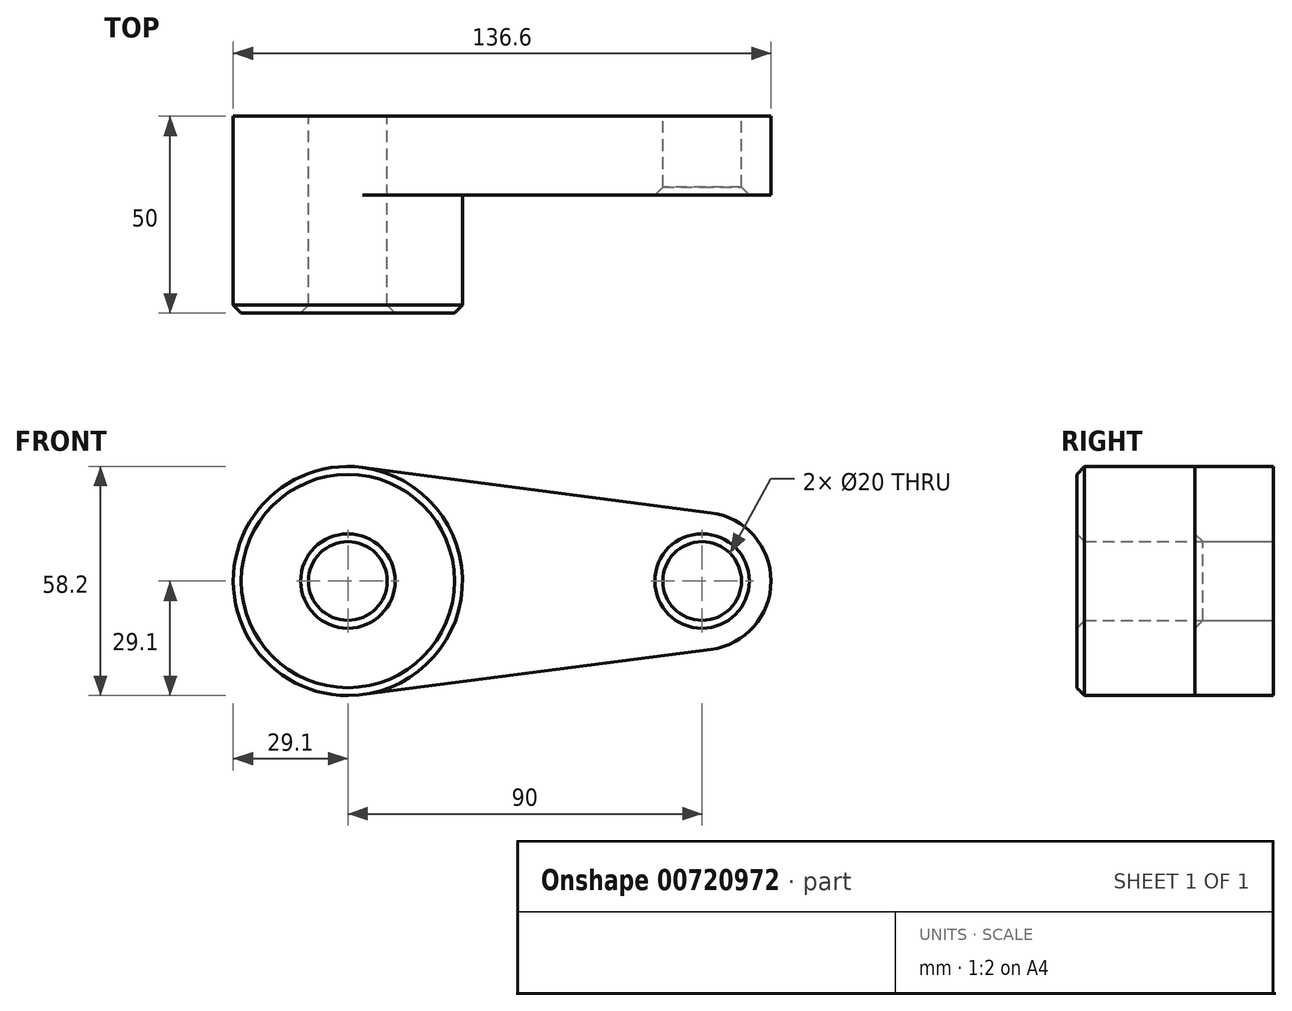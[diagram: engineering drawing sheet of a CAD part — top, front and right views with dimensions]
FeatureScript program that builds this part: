
annotation { "Feature Type Name" : "Feature", "Feature Type Description" : "" }
export const myFeature = defineFeature(function(context is Context, id is Id, definition is map)
    precondition{}
    {
        {
            var Q0;
            Q0=qCreatedBy(makeId("Front.planeOp"),FACE);
            var sketch = newSketch(context, id + "F0", { "sketchPlane" : qUnion([Q0])});
            skCircle(sketch, "E0", {"center": v(0, 0) * mm, "radius": 29.1 * mm});
            skCircle(sketch, "E1", {"center": v(90, 0) * mm, "radius": 17.5 * mm});
            skLineSegment(sketch, "E2", {"start": v(3.75, 28.86) * mm, "end": v(92.26, 17.35) * mm});
            skLineSegment(sketch, "E3", {"start": v(3.75, -28.86) * mm, "end": v(92.26, -17.35) * mm});
            skCircle(sketch, "E4", {"center": v(0, 0) * mm, "radius": 10 * mm});
            skCircle(sketch, "E5", {"center": v(90, 0) * mm, "radius": 10 * mm});
            skSolve(sketch);
        }
        {
            var Q0;
            Q0=makeQuery(id+"F0.imprint","IMPRINT",FACE,{"disambiguationData":[TD([[makeQuery(id+"F0.imprint","IMPRINT",EDGE,{"derivedFrom":sQuery(id+"F0.wireOp",EDGE,"E4")}),-1.0]])]});
            var Q1;
            {var subQ0=sQuery(id+"F0.wireOp",EDGE,"E2");Q1=makeQuery(id+"F0.imprint","IMPRINT",FACE,{"disambiguationData":[TD([[makeQuery(id+"F0.imprint","IMPRINT",EDGE,{"derivedFrom":subQ0}),-1.0]])]});}
            var Q2;
            Q2=makeQuery(id+"F0.imprint","IMPRINT",FACE,{"disambiguationData":[TD([[makeQuery(id+"F0.imprint","IMPRINT",EDGE,{"derivedFrom":sQuery(id+"F0.wireOp",EDGE,"E5")}),-1.0]])]});
            extrude(context, id + "F1", {"entities" : qUnion([Q0, Q1, Q2]), "depth" : 20 * mm, "offsetDistance" : 25.4 * mm});
        }
        {
            var Q0;
            Q0=makeQuery(id+"F0.imprint","IMPRINT",FACE,{"disambiguationData":[TD([[makeQuery(id+"F0.imprint","IMPRINT",EDGE,{"derivedFrom":sQuery(id+"F0.wireOp",EDGE,"E4")}),-1.0]])]});
            extrude(context, id + "F2", {"entities" : qUnion([Q0]), "operationType" : NewBodyOperationType.ADD, "depth" : 50 * mm, "offsetDistance" : 25.4 * mm});
        }
        {
            var Q0;
            Q0=makeQuery(id+"F1.opExtrude","CAP_EDGE",EDGE,{"disambiguationData":[OSD([sQuery(id+"F0.wireOp",EDGE,"E5")])],"isStart":false});
            var Q1;
            Q1=makeQuery(id+"F2.opExtrude","CAP_EDGE",EDGE,{"disambiguationData":[OSD([sQuery(id+"F0.wireOp",EDGE,"E4")])],"isStart":false});
            var Q2;
            Q2=makeQuery(id+"F2.opExtrude","CAP_EDGE",EDGE,{"disambiguationData":[OSD([sQuery(id+"F0.wireOp",EDGE,"E0")])],"isStart":false});
            chamfer(context, id + "F3", {"entities" : qUnion([Q0, Q1, Q2]), "width" : 2 * mm, "tangentPropagation" : true});
        }
    });
